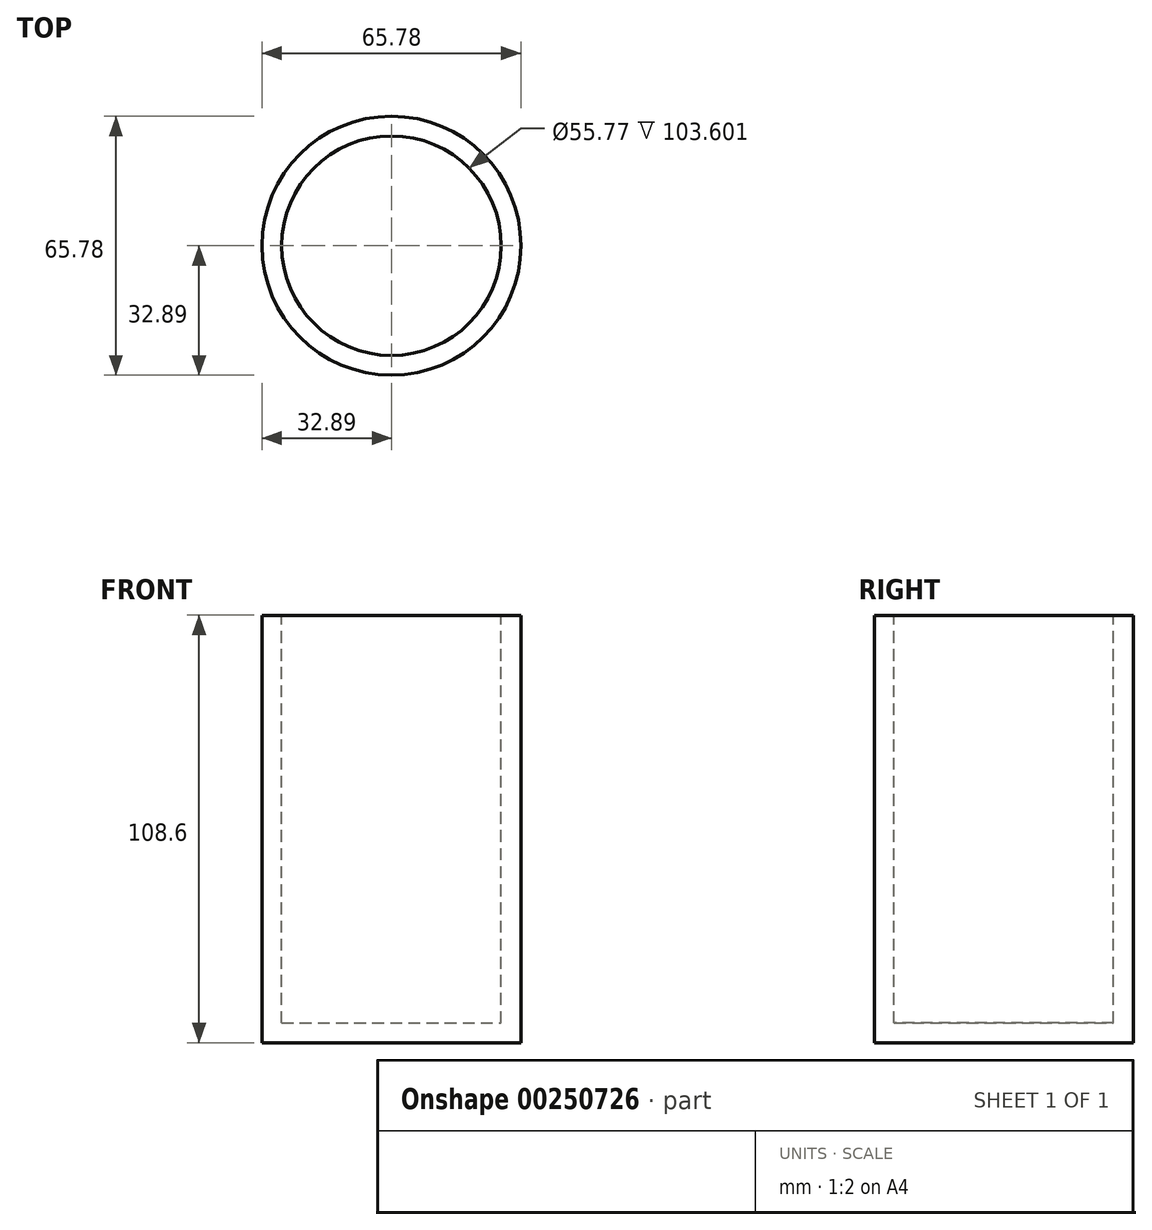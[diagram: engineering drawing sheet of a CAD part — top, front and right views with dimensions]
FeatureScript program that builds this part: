
annotation { "Feature Type Name" : "Feature", "Feature Type Description" : "" }
export const myFeature = defineFeature(function(context is Context, id is Id, definition is map)
    precondition{}
    {
        {
            var Q0;
            Q0=qCreatedBy(makeId("Front.planeOp"),FACE);
            var sketch = newSketch(context, id + "F0", { "sketchPlane" : qUnion([Q0])});
            skLineSegment(sketch, "E0.bottom", {"start": v(-32.89, 50.03) * mm, "end": v(32.89, 50.03) * mm});
            skLineSegment(sketch, "E0.top", {"start": v(-32.89, -58.57) * mm, "end": v(32.89, -58.57) * mm});
            skLineSegment(sketch, "E0.left", {"start": v(-32.89, 50.03) * mm, "end": v(-32.89, -58.57) * mm});
            skLineSegment(sketch, "E0.right", {"start": v(32.89, 50.03) * mm, "end": v(32.89, -58.57) * mm});
            skLineSegment(sketch, "E1", {"start": v(0, 50.03) * mm, "end": v(0, -58.57) * mm});
            skSolve(sketch);
        }
        {
            var Q0;
            {var subQ0=sQuery(id+"F0.wireOp",EDGE,"E0.left");Q0=makeQuery(id+"F0.imprint","IMPRINT",FACE,{"disambiguationData":[TD([[makeQuery(id+"F0.imprint","IMPRINT",EDGE,{"derivedFrom":subQ0}),1.0]])]});}
            var Q1;
            Q1=sQuery(id+"F0.wireOp",EDGE,"E1");
            revolve(context, id + "F1", {"entities" : qUnion([Q0]), "axis" : qUnion([Q1]), "revolveType" : RevolveType.FULL});
        }
        {
            var Q0;
            Q0=makeQuery(id+"F1.opRevolve","SWEPT_FACE",FACE,{"disambiguationData":[OSD([sQuery(id+"F0.wireOp",EDGE,"E0.bottom")])]});
            shell(context, id + "F2", {"entities" : qUnion([Q0]), "thickness" : 5 * mm});
        }
    });
